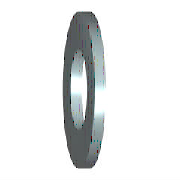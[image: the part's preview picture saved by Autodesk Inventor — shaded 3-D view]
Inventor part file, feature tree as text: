
AUTODESK INVENTOR PART (.ipt)
format: ipt  version: 2015 SP2 (Build 190223200, 223)  size: 105,472 bytes
history: native  units: mm (DEFAULTED — no unit token found)
features: other x1, plane x1, sketch x1
ambient origin geometry x7: Origin, YZ Plane, XY Plane, X Axis, Y Axis, Z Axis, Center Point
bodies: Solid1 (feature_tree), Body (feature_tree)
feature tree (3):
  other  "Work Axis1"
  plane  "Work Plane1"
  sketch  "Sketch"  dims[d0=4.0mm d1=8.0mm d2=1.0mm d3=0.0mm d4=0.0mm d5=0.0mm d6=0.0mm d7=0.0mm]
